# Revit family: WC MIURA16 TCC
name_source: partatom
category: Aparatos sanitarios
units: mm (PartAtom-declared; Revit-internal decimal feet)

## family parameters
Compartido = Sí
Corte con vacíos al cargar = No
Cota de conector redondo = Diámetro de uso
Número OmniClass = 23.45.00.00
Punto de cálculo de habitación = No
Se basa en plano de trabajo = Sí
Siempre vertical = Sí
Tipo de pieza = Normal
Título OmniClass = Sanitary, Laundry, and Cleaning Equipment

## types (1)
- WC MIURA16 TCC
    Accessories = Llave de 7/16", Kit de fijación al piso, Asiento y kit de sujeción, Kit de sujeción y acoplamiento para tanque, Extensión de Ø 15/16"-14 NS-1
    Características del Producto = Diseño ergonómico de labio elongado, espesor
de cerámica de 10 mm, sistema de descarga
tipo Turvex. Activación con sensor y con botón
mecánico.
    Cerámica = Cerámica porcelanizada de alto brillo. Calidad "A", tipo I
    Comentarios de tipo = ELECTRÓNICO: Distancia de detección 25mm a 40mm
Energía: Para el Módulo de Control - 6Vcc (4 baterías alcalinas AA). Para el Sensor - 4,5Vcc (3 baterías alcalinas AAA).
    Conexión de Alimentación = A la alimentacion Ø15/16-14 NS-1
    Conexión de Descarga = A la descarga se acopla al Ø de drenaje de 4" con brida sanitaria o cuello de cera.
    Descripción = Inodoro Elongado, Trampa Oculta, Tecnología Cero Contacto de Baterías con Botón
de Sensor Independiente y Botón de Descarga Manual 4,8 l, Blanco.
    Elevación por defecto = 0.0"
    Fabricante = Helvex S.A. de C.V.
    Maximum Consumption = 4,8 lpd
    Modelo = WC MIURA16 TCC
    Operation = Para activar la descarga debe de generar un movimiento oscilatorio enfrente del sensor. El
producto tiene un botón mecánico de accionamiento manual.
    Presión Máxima de Trabajo = 85.3 psi
    Presión Mínima de Trabajo = 11.3 psi
    Valves = Valv. de admisión y descarga certificadas, Valv. de admisión silenciosa, válvulas armadas y calibradas, válvula de descarga con sello hermético

## geometry (parser evidence)
native form markers: Sweep x3
no freeform markers — native parametric forms only
